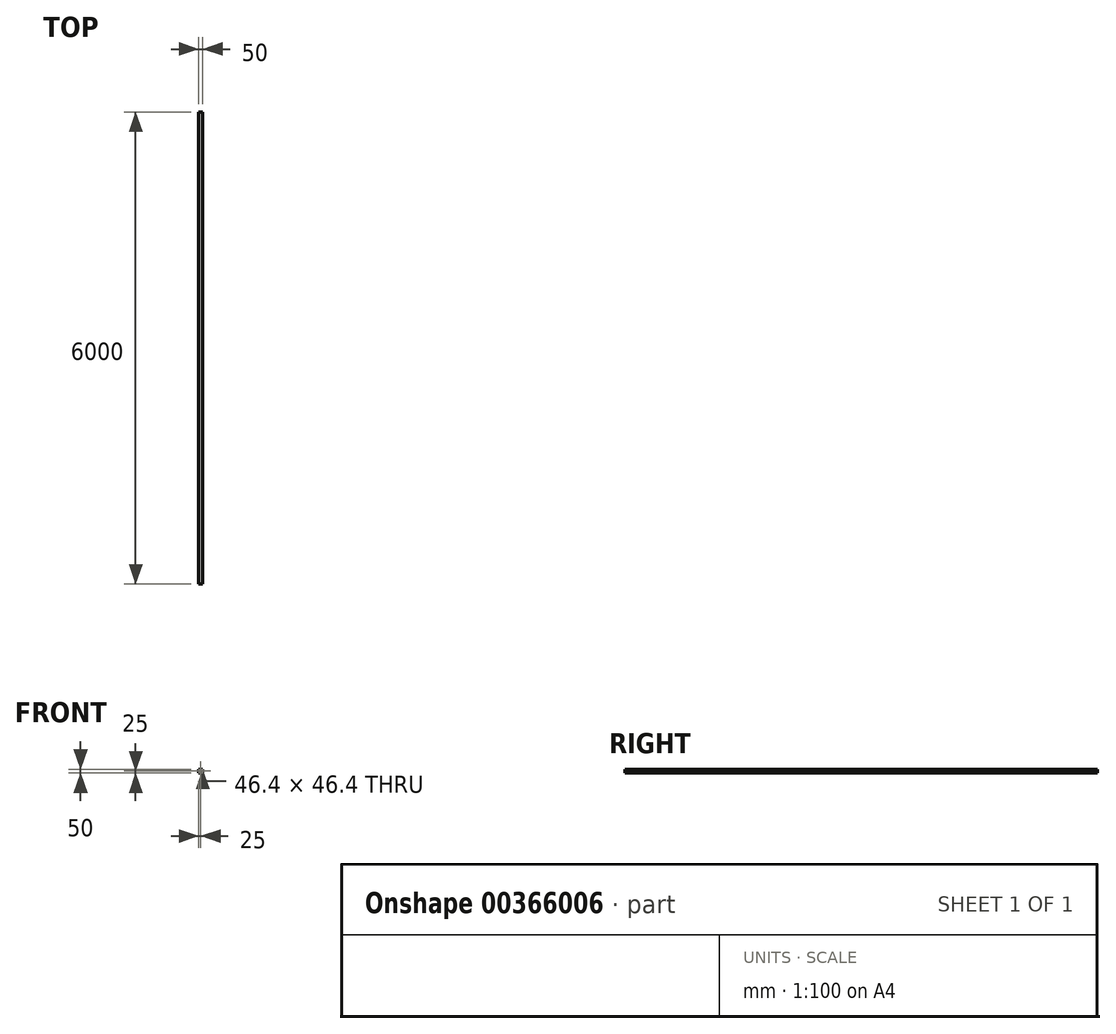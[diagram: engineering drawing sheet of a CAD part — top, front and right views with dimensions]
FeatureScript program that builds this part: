
annotation { "Feature Type Name" : "Feature", "Feature Type Description" : "" }
export const myFeature = defineFeature(function(context is Context, id is Id, definition is map)
    precondition{}
    {
        {
            var Q0;
            Q0=qCreatedBy(makeId("Front.planeOp"),FACE);
            var sketch = newSketch(context, id + "F0", { "sketchPlane" : qUnion([Q0])});
            skLineSegment(sketch, "E0.bottom", {"start": v(0, 0) * mm, "end": v(50, 0) * mm});
            skLineSegment(sketch, "E0.top", {"start": v(0, 50) * mm, "end": v(50, 50) * mm});
            skLineSegment(sketch, "E0.left", {"start": v(0, 0) * mm, "end": v(0, 50) * mm});
            skLineSegment(sketch, "E0.right", {"start": v(50, 0) * mm, "end": v(50, 50) * mm});
            skLineSegment(sketch, "E1.0", {"start": v(1.8, 48.2) * mm, "end": v(48.2, 48.2) * mm});
            skLineSegment(sketch, "E1.1", {"start": v(1.8, 1.8) * mm, "end": v(1.8, 48.2) * mm});
            skLineSegment(sketch, "E1.2", {"start": v(1.8, 1.8) * mm, "end": v(48.2, 1.8) * mm});
            skLineSegment(sketch, "E1.3", {"start": v(48.2, 1.8) * mm, "end": v(48.2, 48.2) * mm});
            skSolve(sketch);
        }
        {
            var Q0;
            Q0 = qSketchRegion(id + "F0", true);
            extrude(context, id + "F1", {"entities" : qUnion([Q0]), "depth" : 6000 * mm});
        }
    });
